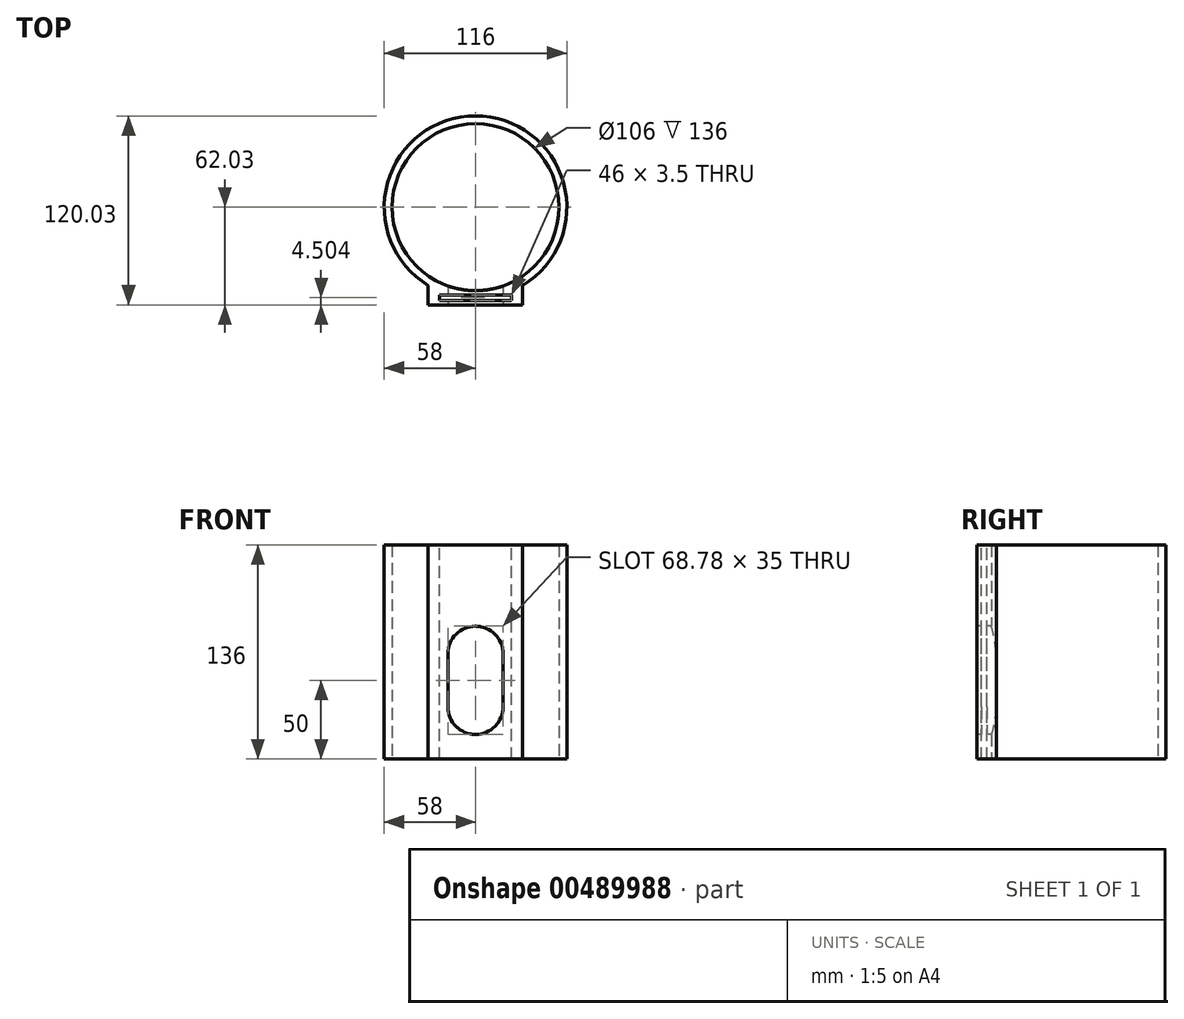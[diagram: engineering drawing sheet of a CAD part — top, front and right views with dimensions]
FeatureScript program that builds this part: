
annotation { "Feature Type Name" : "Feature", "Feature Type Description" : "" }
export const myFeature = defineFeature(function(context is Context, id is Id, definition is map)
    precondition{}
    {
        {
            var Q0;
            Q0=qCreatedBy(makeId("Top.planeOp"),FACE);
            var sketch = newSketch(context, id + "F0", { "sketchPlane" : qUnion([Q0])});
            skCircle(sketch, "E0", {"center": v(0, 0) * mm, "radius": 53 * mm});
            skCircle(sketch, "E1", {"center": v(0, 0) * mm, "radius": 58 * mm});
            skSolve(sketch);
        }
        {
            var Q0;
            Q0 = qSketchRegion(id + "F0", true);
            extrude(context, id + "F1", {"entities" : qUnion([Q0]), "depth" : 136 * mm});
        }
        {
            var Q0;
            Q0=qCreatedBy(makeId("Top.planeOp"),FACE);
            var sketch = newSketch(context, id + "F2", { "sketchPlane" : qUnion([Q0])});
            skLineSegment(sketch, "E2", {"start": v(-30, -45.95) * mm, "end": v(-30, -62.03) * mm});
            skLineSegment(sketch, "E3", {"start": v(-30, -62.03) * mm, "end": v(30, -62.03) * mm});
            skLineSegment(sketch, "E4", {"start": v(30, -62.03) * mm, "end": v(30, -47.67) * mm});
            skLineSegment(sketch, "E5", {"start": v(30, -47.67) * mm, "end": v(6.97, -54.73) * mm});
            skLineSegment(sketch, "E6", {"start": v(6.97, -54.73) * mm, "end": v(-8.05, -54.73) * mm});
            skLineSegment(sketch, "E7", {"start": v(-8.05, -54.73) * mm, "end": v(-30, -45.95) * mm});
            skPoint(sketch, "E8", {"position": v(0, -62.03) * mm});
            skSolve(sketch);
        }
        {
            var Q0;
            Q0 = qSketchRegion(id + "F2", true);
            extrude(context, id + "F3", {"entities" : qUnion([Q0]), "operationType" : NewBodyOperationType.ADD, "depth" : 136 * mm});
        }
        {
            var Q0;
            Q0=makeQuery(id+"F3.opExtrude","SWEPT_FACE",FACE,{"disambiguationData":[OSD([sQuery(id+"F2.wireOp",EDGE,"E3")])]});
            var sketch = newSketch(context, id + "F4", { "sketchPlane" : qUnion([Q0])});
            skLineSegment(sketch, "E9.bottom", {"start": v(17.5, 66.89) * mm, "end": v(-17.5, 66.89) * mm});
            skLineSegment(sketch, "E9.top", {"start": v(17.5, 33.11) * mm, "end": v(-17.5, 33.11) * mm});
            skLineSegment(sketch, "E9.left", {"start": v(17.5, 66.89) * mm, "end": v(17.5, 33.11) * mm});
            skLineSegment(sketch, "E9.right", {"start": v(-17.5, 66.89) * mm, "end": v(-17.5, 33.11) * mm});
            skPoint(sketch, "E9.middle", {"position": v(0, 50) * mm});
            skLineSegment(sketch, "E10", {"start": v(0, 0) * mm, "end": v(0, 50) * mm, "construction": true});
            skArc(sketch, "E11", {"start": v(-17.5, 33.11) * mm, "mid": v(0, 15.61) * mm, "end": v(17.5, 33.11) * mm});
            skArc(sketch, "E12", {"start": v(17.5, 66.89) * mm, "mid": v(0, 84.39) * mm, "end": v(-17.5, 66.89) * mm});
            skSolve(sketch);
        }
        {
            var Q0;
            Q0 = qSketchRegion(id + "F4", true);
            extrude(context, id + "F5", {"entities" : qUnion([Q0]), "operationType" : NewBodyOperationType.REMOVE, "oppositeDirection" : true, "depth" : 25 * mm});
        }
        {
            var Q0;
            Q0=makeQuery(id+"F3.boolean.opBoolean","MERGE",FACE,{"derivedFrom":[makeQuery(id+"F1.opExtrude","CAP_FACE",FACE,{"disambiguationData":[OSD([sQuery(id+"F0.wireOp",EDGE,"E0"),sQuery(id+"F0.wireOp",EDGE,"E1")])],"isStart":false}),makeQuery(id+"F3.opExtrude","CAP_FACE",FACE,{"disambiguationData":[OSD([sQuery(id+"F2.wireOp",EDGE,"E2"),sQuery(id+"F2.wireOp",EDGE,"E3"),sQuery(id+"F2.wireOp",EDGE,"E4"),sQuery(id+"F2.wireOp",EDGE,"E5"),sQuery(id+"F2.wireOp",EDGE,"E6"),sQuery(id+"F2.wireOp",EDGE,"E7")])],"isStart":false})]});
            var sketch = newSketch(context, id + "F6", { "sketchPlane" : qUnion([Q0])});
            skLineSegment(sketch, "E13", {"start": v(0, -62.03) * mm, "end": v(0, -57.53) * mm, "construction": true});
            skLineSegment(sketch, "E14.bottom", {"start": v(-23, -55.78) * mm, "end": v(23, -55.78) * mm});
            skLineSegment(sketch, "E14.top", {"start": v(-23, -59.28) * mm, "end": v(23, -59.28) * mm});
            skLineSegment(sketch, "E14.left", {"start": v(-23, -55.78) * mm, "end": v(-23, -59.28) * mm});
            skLineSegment(sketch, "E14.right", {"start": v(23, -55.78) * mm, "end": v(23, -59.28) * mm});
            skPoint(sketch, "E14.middle", {"position": v(0, -57.53) * mm});
            skSolve(sketch);
        }
        {
            var Q0;
            Q0 = qSketchRegion(id + "F6", true);
            extrude(context, id + "F7", {"entities" : qUnion([Q0]), "operationType" : NewBodyOperationType.REMOVE, "oppositeDirection" : true, "depth" : 136 * mm});
        }
    });
